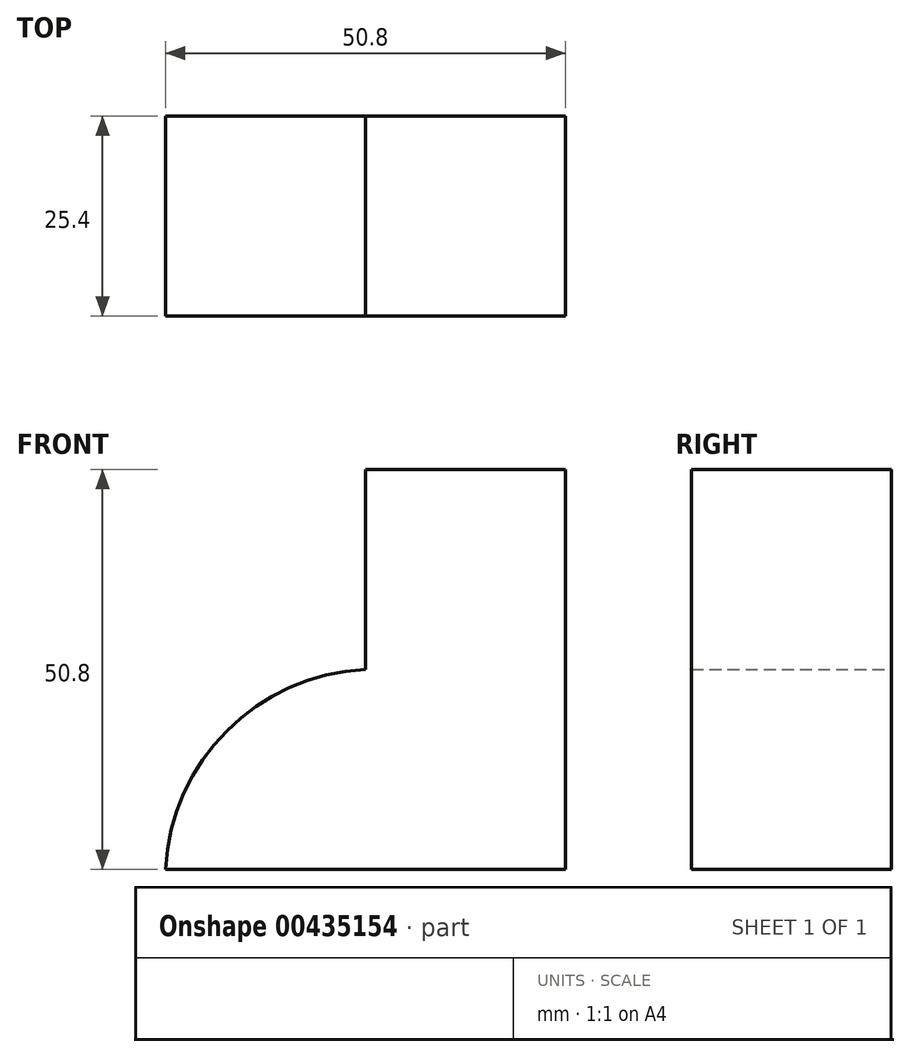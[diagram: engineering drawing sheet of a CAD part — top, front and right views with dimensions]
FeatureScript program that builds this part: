
annotation { "Feature Type Name" : "Feature", "Feature Type Description" : "" }
export const myFeature = defineFeature(function(context is Context, id is Id, definition is map)
    precondition{}
    {
        {
            var Q0;
            Q0=qCreatedBy(makeId("Front.planeOp"),FACE);
            var sketch = newSketch(context, id + "F0", { "sketchPlane" : qUnion([Q0])});
            skLineSegment(sketch, "E0", {"start": v(-46.21, 54.23) * mm, "end": v(-20.81, 54.23) * mm});
            skLineSegment(sketch, "E1", {"start": v(-46.21, 54.23) * mm, "end": v(-46.21, 28.83) * mm});
            skLineSegment(sketch, "E2", {"start": v(-20.81, 54.23) * mm, "end": v(-20.81, 3.43) * mm});
            skLineSegment(sketch, "E3", {"start": v(-20.81, 3.43) * mm, "end": v(-71.61, 3.43) * mm});
            skArc(sketch, "E4", {"start": v(-46.21, 28.83) * mm, "mid": v(-63.83, 21.05) * mm, "end": v(-71.61, 3.43) * mm});
            skSolve(sketch);
        }
        {
            var Q0;
            Q0 = qSketchRegion(id + "F0", true);
            extrude(context, id + "F1", {"entities" : qUnion([Q0]), "depth" : 25.4 * mm});
        }
    });
